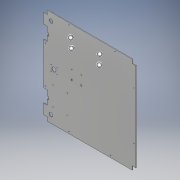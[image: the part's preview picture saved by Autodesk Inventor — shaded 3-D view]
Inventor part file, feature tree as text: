
AUTODESK INVENTOR PART (.ipt)
format: ipt  version: 2019 (Build 230136000, 136)  size: 368,640 bytes
history: native  units: mm
features: sketch x8, extrude x4, other x4, mirror x1, fillet x1, hole x1
ambient origin geometry x8: Origin, YZ Plane, XZ Plane, XY Plane, X Axis, Y Axis, Z Axis, Center Point
bodies: Body1 (feature_tree)
feature tree (19):
  extrude  "Extrusion2"  Depth=490.0mm
  extrude  "Extrusion3"  Depth=3.0mm TaperAngle=0.0deg
  extrude  "Extrusion4"  Depth=10.0mm
  extrude  "Extrusion5"  Depth=4.2mm
  mirror  "Mirror1"
  fillet  "Fillet1"  Radius=4.2mm
  hole  "Hole1"  [1 undecoded]
  sketch  "Sketch1"  dims[d0=510.0mm d1=490.0mm]
  sketch  "Sketch2"  dims[d2=20.0mm d5=3.0mm d6=0.0mm]
  sketch  "Sketch3"  dims[d7=10.0mm d8=10.0mm]
  sketch  "Sketch4"  dims[d9=117.5mm d10=100.0mm d11=4.2mm]
  sketch  "Sketch6"  dims[d12=3.0mm d13=0.0mm d14=40.0mm]
  sketch  "Sketch7"  dims[d15=22.0mm]
  sketch  "Sketch8"  dims[d16=31.0mm]
  sketch  "Sketch9"  dims[d17=3.4mm d18=10.0mm d19=0.0mm d21=70.5mm d22=12.5mm d23=8.5mm d24=10.0mm d25=0.0mm d26=1.0mm d27=147.0mm d28=20.0mm d29=88.5mm d30=50.0mm d31=150.0mm d32=4.2mm d33=70.0mm d34=140.0mm d35=4.2mm d36=8.0mm d37=3.023mm d38=2.0mm d39=14.3117mm d40=3.0mm d41=20.594885mm d42=0.0mm d43=0.0mm d44=0.0mm d45=0.0mm d46=0.0mm d47=0.0mm d48=0.0mm d49=0.0mm d50=20.0mm d51=40.0mm d52=20.0mm d53=3.0mm d54=3.0mm d55=0.0mm d56=50.0mm d57=62.0mm d58=45.53mm d59=7.62mm d60=5.0mm d61=4.2mm d63=3.0mm d64=0.0mm d66=200.0mm d67=175.0mm d68=101.8mm d69=75.8mm d71=3.4mm d72=3.0mm d73=0.0mm d74=80.0mm d75=50.0mm]
  other  "Cut1"
  other  "Cut2"
  other  "Cut3"
  other  "Definition1"
note: 1 required parameter value undecoded (feature->parameter linkage not recoverable at this tier; creation-order binding heuristic only, values carry confidence <= 0.55)
